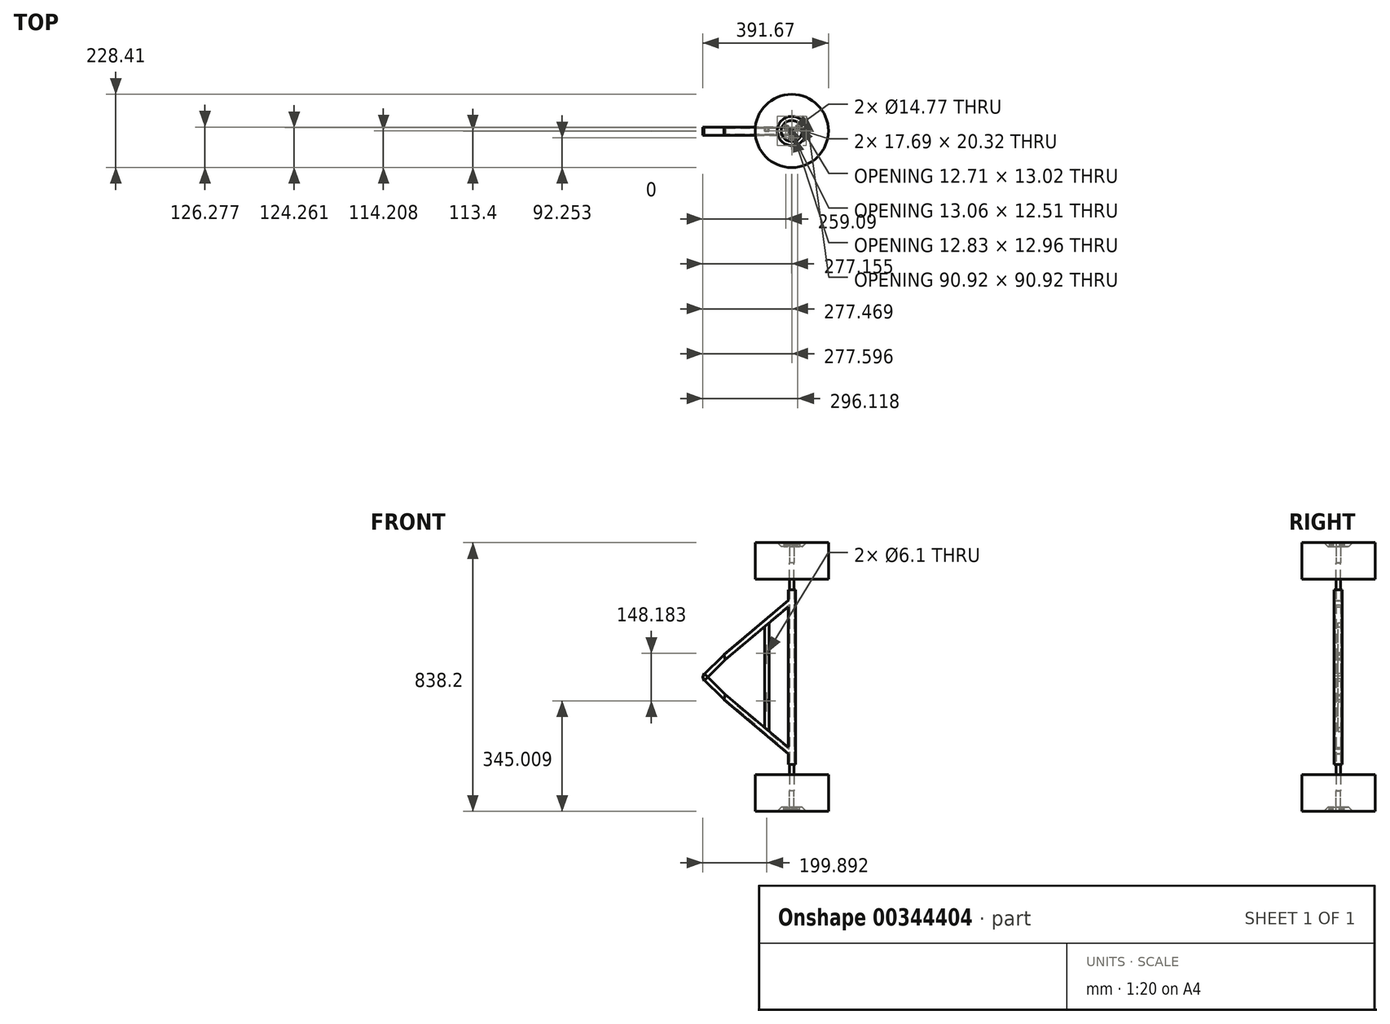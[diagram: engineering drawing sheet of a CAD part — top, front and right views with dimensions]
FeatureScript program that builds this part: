
annotation { "Feature Type Name" : "Feature", "Feature Type Description" : "" }
export const myFeature = defineFeature(function(context is Context, id is Id, definition is map)
    precondition{}
    {
        {
            var Q0;
            Q0=qCreatedBy(makeId("Front.planeOp"),FACE);
            var sketch = newSketch(context, id + "F0", { "sketchPlane" : qUnion([Q0])});
            skLineSegment(sketch, "E0", {"start": v(0, 0) * mm, "end": v(0, 258.28) * mm});
            skLineSegment(sketch, "E1", {"start": v(0, 258.28) * mm, "end": v(-222.38, 70.18) * mm});
            skLineSegment(sketch, "E2.MirrorCS", {"start": v(0, 0) * mm, "end": v(0, -258.28) * mm});
            skLineSegment(sketch, "E3.MirrorCS", {"start": v(0, -258.28) * mm, "end": v(-222.38, -70.18) * mm});
            skLineSegment(sketch, "E4", {"start": v(-22.77, 239.03) * mm, "end": v(-22.77, -239.03) * mm});
            skLineSegment(sketch, "E5", {"start": v(-218.72, 53.72) * mm, "end": v(-22.77, 219.42) * mm});
            skLineSegment(sketch, "E6.MirrorCS", {"start": v(-218.72, -53.72) * mm, "end": v(-22.77, -219.42) * mm});
            skLineSegment(sketch, "E7", {"start": v(-222.38, 70.18) * mm, "end": v(-218.72, 53.72) * mm});
            skLineSegment(sketch, "E8", {"start": v(-218.72, -53.72) * mm, "end": v(-222.38, -70.18) * mm});
            skLineSegment(sketch, "E9", {"start": v(-22.77, 239.03) * mm, "end": v(-22.77, 272.77) * mm});
            skLineSegment(sketch, "E10", {"start": v(-22.77, 272.77) * mm, "end": v(0, 272.77) * mm});
            skLineSegment(sketch, "E11", {"start": v(0, 272.77) * mm, "end": v(0, 258.28) * mm});
            skLineSegment(sketch, "E12.MirrorCS", {"start": v(-22.77, -272.77) * mm, "end": v(0, -272.77) * mm});
            skLineSegment(sketch, "E13.MirrorCS", {"start": v(-22.77, -239.03) * mm, "end": v(-22.77, -272.77) * mm});
            skLineSegment(sketch, "E14.MirrorCS", {"start": v(0, -272.77) * mm, "end": v(0, -258.28) * mm});
            skSolve(sketch);
        }
        {
            var Q0;
            Q0 = qSketchRegion(id + "F0", true);
            extrude(context, id + "F1", {"entities" : qUnion([Q0]), "depth" : 25.4 * mm});
        }
        {
            var Q0;
            Q0=makeQuery(id+"F1.opExtrude","SWEPT_FACE",FACE,{"disambiguationData":[OSD([sQuery(id+"F0.wireOp",EDGE,"E10")])]});
            var Q1;
            Q1=makeQuery(id+"F1.opExtrude","SWEPT_FACE",FACE,{"disambiguationData":[OSD([sQuery(id+"F0.wireOp",EDGE,"E12.MirrorCS")])]});
            shell(context, id + "F2", {"entities" : qUnion([Q0, Q1]), "thickness" : 2.54 * mm});
        }
        {
            var Q0;
            Q0=qCreatedBy(makeId("Top.planeOp"),FACE);
            var sketch = newSketch(context, id + "F3", { "sketchPlane" : qUnion([Q0])});
            skCircle(sketch, "E15", {"center": v(-11.51, -11.9) * mm, "radius": 7.39 * mm});
            skSolve(sketch);
        }
        {
            var Q0;
            Q0=makeQuery(id+"F3.imprint","IMPRINT",FACE,{"disambiguationData":[TD([[makeQuery(id+"F3.imprint","IMPRINT",EDGE,{"derivedFrom":sQuery(id+"F3.wireOp",EDGE,"E15")}),1.0]])]});
            var Q1;
            Q1=sQuery(id+"F3.wireOp",EDGE,"E15");
            extrude(context, id + "F4", {"entities" : qUnion([Q0]), "surfaceEntities" : qUnion([Q1]), "endBound" : BoundingType.SYMMETRIC, "depth" : 711.2 * mm});
        }
        {
            var Q0;
            Q0=makeQuery(id+"F4.opExtrude","CAP_FACE",FACE,{"disambiguationData":[OSD([sQuery(id+"F3.wireOp",EDGE,"E15")])],"isStart":false});
            var sketch = newSketch(context, id + "F5", { "sketchPlane" : qUnion([Q0])});
            skCircle(sketch, "E16", {"center": v(-11.51, -11.9) * mm, "radius": 32.76 * mm});
            skSolve(sketch);
        }
        {
            var Q0;
            Q0=makeQuery(id+"F5.imprint","IMPRINT",FACE,{"disambiguationData":[TD([[makeQuery(id+"F5.imprint","IMPRINT",EDGE,{"derivedFrom":sQuery(id+"F5.wireOp",EDGE,"E16")}),1.0]])]});
            extrude(context, id + "F6", {"entities" : qUnion([Q0]), "operationType" : NewBodyOperationType.ADD, "endBound" : BoundingType.SYMMETRIC, "depth" : 101.6 * mm});
        }
        {
            var Q0;
            Q0=makeQuery(id+"F4.opExtrude","CAP_FACE",FACE,{"disambiguationData":[OSD([sQuery(id+"F3.wireOp",EDGE,"E15")])],"isStart":false});
            var sketch = newSketch(context, id + "F7", { "sketchPlane" : qUnion([Q0])});
            skCircle(sketch, "E17", {"center": v(-11.51, -11.9) * mm, "radius": 7.38 * mm});
            skSolve(sketch);
        }
        {
            var Q0;
            Q0=makeQuery(id+"F7.imprint","IMPRINT",FACE,{"disambiguationData":[TD([[makeQuery(id+"F7.imprint","IMPRINT",EDGE,{"derivedFrom":sQuery(id+"F7.wireOp",EDGE,"E17")}),1.0]])]});
            extrude(context, id + "F8", {"entities" : qUnion([Q0]), "operationType" : NewBodyOperationType.ADD, "depth" : 63.5 * mm});
        }
        {
            var Q0;
            Q0=makeQuery(id+"F6.opExtrude","CAP_FACE",FACE,{"disambiguationData":[OSD([sQuery(id+"F3.wireOp",EDGE,"E15"),sQuery(id+"F5.wireOp",EDGE,"E16")])],"isStart":false});
            var sketch = newSketch(context, id + "F9", { "sketchPlane" : qUnion([Q0])});
            skCircle(sketch, "E18.cCircle", {"center": v(-12.22, -33.58) * mm, "radius": 5.56 * mm, "construction": true});
            skLineSegment(sketch, "E18.0", {"start": v(-9.3, -27.37) * mm, "end": v(-5.4, -34.45) * mm});
            skLineSegment(sketch, "E18.1", {"start": v(-5.4, -34.45) * mm, "end": v(-10.94, -40.33) * mm});
            skLineSegment(sketch, "E18.2", {"start": v(-10.94, -40.33) * mm, "end": v(-18.24, -36.88) * mm});
            skLineSegment(sketch, "E18.3", {"start": v(-18.24, -36.88) * mm, "end": v(-17.22, -28.87) * mm});
            skLineSegment(sketch, "E18.4", {"start": v(-17.22, -28.87) * mm, "end": v(-9.3, -27.37) * mm});
            skPoint(sketch, "E18.0.midPoint", {"position": v(-7.35, -30.9) * mm});
            skLineSegment(sketch, "E19.1.0", {"start": v(-26.02, -6.08) * mm, "end": v(-34.1, -5.9) * mm});
            skLineSegment(sketch, "E19.1.1", {"start": v(-23.36, 1.54) * mm, "end": v(-26.02, -6.08) * mm});
            skCircle(sketch, "E19.1.2", {"center": v(-29.94, -0.43) * mm, "radius": 5.56 * mm, "construction": true});
            skLineSegment(sketch, "E19.1.3", {"start": v(-29.79, 6.43) * mm, "end": v(-23.36, 1.54) * mm});
            skLineSegment(sketch, "E19.1.4", {"start": v(-36.42, 1.83) * mm, "end": v(-29.79, 6.43) * mm});
            skLineSegment(sketch, "E19.1.5", {"start": v(-34.1, -5.9) * mm, "end": v(-36.42, 1.83) * mm});
            skLineSegment(sketch, "E19.2.0", {"start": v(0.78, -2.23) * mm, "end": v(4.97, 4.67) * mm});
            skLineSegment(sketch, "E19.2.1", {"start": v(6.05, -8.35) * mm, "end": v(0.78, -2.23) * mm});
            skCircle(sketch, "E19.2.2", {"center": v(7.63, -1.66) * mm, "radius": 5.56 * mm, "construction": true});
            skLineSegment(sketch, "E19.2.3", {"start": v(13.5, -5.23) * mm, "end": v(6.05, -8.35) * mm});
            skLineSegment(sketch, "E19.2.4", {"start": v(12.83, 2.82) * mm, "end": v(13.5, -5.23) * mm});
            skLineSegment(sketch, "E19.2.5", {"start": v(4.97, 4.67) * mm, "end": v(12.83, 2.82) * mm});
            skPoint(sketch, "E19.center", {"position": v(-11.51, -11.9) * mm});
            skLineSegment(sketch, "E19.anchor1", {"start": v(-11.51, -11.9) * mm, "end": v(-5.4, -34.45) * mm, "construction": true});
            skLineSegment(sketch, "E19.anchor2", {"start": v(-11.51, -11.9) * mm, "end": v(4.97, 4.67) * mm, "construction": true});
            skSolve(sketch);
        }
        {
            var Q0;
            Q0=makeQuery(id+"F9.imprint","IMPRINT",FACE,{"disambiguationData":[TD([[makeQuery(id+"F9.imprint","IMPRINT",EDGE,{"derivedFrom":sQuery(id+"F9.wireOp",EDGE,"E18.0")}),-1.0]])]});
            var Q1;
            Q1=makeQuery(id+"F9.imprint","IMPRINT",FACE,{"disambiguationData":[TD([[makeQuery(id+"F9.imprint","IMPRINT",EDGE,{"derivedFrom":sQuery(id+"F9.wireOp",EDGE,"E19.2.0")}),-1.0]])]});
            var Q2;
            Q2=makeQuery(id+"F9.imprint","IMPRINT",FACE,{"disambiguationData":[TD([[makeQuery(id+"F9.imprint","IMPRINT",EDGE,{"derivedFrom":sQuery(id+"F9.wireOp",EDGE,"E19.1.0")}),-1.0]])]});
            extrude(context, id + "F10", {"entities" : qUnion([Q0, Q1, Q2]), "operationType" : NewBodyOperationType.ADD, "depth" : 7.62 * mm});
        }
        {
            var Q0;
            Q0=makeQuery(id+"F6.opExtrude","CAP_FACE",FACE,{"disambiguationData":[OSD([sQuery(id+"F3.wireOp",EDGE,"E15"),sQuery(id+"F5.wireOp",EDGE,"E16")])],"isStart":true});
            var sketch = newSketch(context, id + "F11", { "sketchPlane" : qUnion([Q0])});
            skCircle(sketch, "E20", {"center": v(-11.51, 11.9) * mm, "radius": 114.2 * mm});
            skCircle(sketch, "E21", {"center": v(-11.51, 11.9) * mm, "radius": 90.4 * mm});
            skSolve(sketch);
        }
        {
            var Q0;
            Q0=makeQuery(id+"F11.imprint","IMPRINT",FACE,{"disambiguationData":[TD([[makeQuery(id+"F11.imprint","IMPRINT",EDGE,{"derivedFrom":sQuery(id+"F11.wireOp",EDGE,"E20")}),1.0]])]});
            var Q1;
            Q1=makeQuery(id+"F11.imprint","IMPRINT",FACE,{"disambiguationData":[TD([[makeQuery(id+"F11.imprint","IMPRINT",EDGE,{"derivedFrom":sQuery(id+"F11.wireOp",EDGE,"E21")}),1.0]])]});
            extrude(context, id + "F12", {"entities" : qUnion([Q0, Q1]), "operationType" : NewBodyOperationType.ADD, "oppositeDirection" : true, "depth" : 114.3 * mm});
        }
        {
            var Q0;
            Q0=makeQuery(id+"F12.opExtrude","CAP_EDGE",EDGE,{"disambiguationData":[OSD([sQuery(id+"F5.wireOp",EDGE,"E16")])],"isStart":false});
            chamfer(context, id + "F13", {"entities" : qUnion([Q0]), "width" : 12.7 * mm, "tangentPropagation" : true});
        }
        {
            var Q0;
            Q0=makeQuery(id+"F4.opExtrude","SWEPT_BODY",BODY,{"disambiguationData":[OSD([sQuery(id+"F3.wireOp",EDGE,"E15")])]});
            var Q1;
            Q1=qCreatedBy(makeId("Top.planeOp"),FACE);
            mirror(context, id + "F14", {"operationType" : NewBodyOperationType.ADD, "entities" : qUnion([Q0]), "mirrorPlane" : qUnion([Q1])});
        }
        {
            var Q0;
            Q0=qCreatedBy(makeId("Front.planeOp"),FACE);
            var sketch = newSketch(context, id + "F15", { "sketchPlane" : qUnion([Q0])});
            skLineSegment(sketch, "E22", {"start": v(-221.44, 66.17) * mm, "end": v(-288.08, 0) * mm});
            skLineSegment(sketch, "E23.MirrorCS", {"start": v(-221.44, -66.17) * mm, "end": v(-288.08, 0) * mm});
            skSolve(sketch);
        }
        {
            var Q0;
            Q0=makeQuery(id+"F1.opExtrude","SWEPT_FACE",FACE,{"disambiguationData":[OSD([sQuery(id+"F0.wireOp",EDGE,"E7")])]});
            var Q1;
            Q1=sQuery(id+"F15.wireOp",EDGE,"E22");
            sweep(context, id + "F16", {"operationType" : NewBodyOperationType.ADD, "profiles" : qUnion([Q0]), "path" : qUnion([Q1])});
        }
        {
            var Q0;
            Q0=makeQuery(id+"F1.opExtrude","SWEPT_BODY",BODY,{"disambiguationData":[OSD([sQuery(id+"F0.wireOp",EDGE,"E0"),sQuery(id+"F0.wireOp",EDGE,"E1"),sQuery(id+"F0.wireOp",EDGE,"E2.MirrorCS"),sQuery(id+"F0.wireOp",EDGE,"E3.MirrorCS"),sQuery(id+"F0.wireOp",EDGE,"E4"),sQuery(id+"F0.wireOp",EDGE,"E5"),sQuery(id+"F0.wireOp",EDGE,"E6.MirrorCS"),sQuery(id+"F0.wireOp",EDGE,"E7"),sQuery(id+"F0.wireOp",EDGE,"E8"),sQuery(id+"F0.wireOp",EDGE,"E9"),sQuery(id+"F0.wireOp",EDGE,"E10"),sQuery(id+"F0.wireOp",EDGE,"E11"),sQuery(id+"F0.wireOp",EDGE,"E12.MirrorCS"),sQuery(id+"F0.wireOp",EDGE,"E13.MirrorCS"),sQuery(id+"F0.wireOp",EDGE,"E14.MirrorCS")])]});
            var Q1;
            Q1=qCreatedBy(makeId("Top.planeOp"),FACE);
            mirror(context, id + "F17", {"entities" : qUnion([Q0]), "mirrorPlane" : qUnion([Q1])});
        }
        {
            var Q0;
            Q0=qCreatedBy(makeId("Front.planeOp"),FACE);
            var sketch = newSketch(context, id + "F18", { "sketchPlane" : qUnion([Q0])});
            skLineSegment(sketch, "E24", {"start": v(-82.14, -169.23) * mm, "end": v(-82.14, 0) * mm});
            skLineSegment(sketch, "E25", {"start": v(-96.27, -156.85) * mm, "end": v(-96.27, 0) * mm});
            skLineSegment(sketch, "E26", {"start": v(-96.27, -156.85) * mm, "end": v(-82.14, -169.23) * mm});
            skLineSegment(sketch, "E27.MirrorCS", {"start": v(-82.14, 169.23) * mm, "end": v(-82.14, 0) * mm});
            skLineSegment(sketch, "E28.MirrorCS", {"start": v(-96.27, 156.85) * mm, "end": v(-96.27, 0) * mm});
            skLineSegment(sketch, "E29.MirrorCS", {"start": v(-96.27, 156.85) * mm, "end": v(-82.14, 169.23) * mm});
            skSolve(sketch);
        }
        {
            var Q0;
            Q0=makeQuery(id+"F18.imprint","IMPRINT",FACE,{"disambiguationData":[TD([[makeQuery(id+"F18.imprint","IMPRINT",EDGE,{"derivedFrom":sQuery(id+"F18.wireOp",EDGE,"E24")}),1.0]])]});
            extrude(context, id + "F19", {"entities" : qUnion([Q0]), "depth" : 12.7 * mm});
        }
        {
            var Q0;
            Q0=makeQuery(id+"F19.opExtrude","CAP_FACE",FACE,{"disambiguationData":[OSD([sQuery(id+"F18.wireOp",EDGE,"E24"),sQuery(id+"F18.wireOp",EDGE,"E25"),sQuery(id+"F18.wireOp",EDGE,"E26"),sQuery(id+"F18.wireOp",EDGE,"E27.MirrorCS"),sQuery(id+"F18.wireOp",EDGE,"E28.MirrorCS"),sQuery(id+"F18.wireOp",EDGE,"E29.MirrorCS")])],"isStart":true});
            var sketch = newSketch(context, id + "F20", { "sketchPlane" : qUnion([Q0])});
            skCircle(sketch, "E30", {"center": v(89.09, -74.1) * mm, "radius": 3.08 * mm});
            skCircle(sketch, "E31.MirrorC", {"center": v(89.09, 74.1) * mm, "radius": 3.08 * mm});
            skSolve(sketch);
        }
        {
            var Q0;
            Q0=sQuery(id+"F20.wireOp",VERTEX,"E30.center");
            var Q1;
            Q1=sQuery(id+"F20.wireOp",VERTEX,"E31.MirrorC.center");
            var Q2;
            Q2=makeQuery(id+"F19.opExtrude","SWEPT_BODY",BODY,{"disambiguationData":[OSD([sQuery(id+"F18.wireOp",EDGE,"E24"),sQuery(id+"F18.wireOp",EDGE,"E25"),sQuery(id+"F18.wireOp",EDGE,"E26"),sQuery(id+"F18.wireOp",EDGE,"E27.MirrorCS"),sQuery(id+"F18.wireOp",EDGE,"E28.MirrorCS"),sQuery(id+"F18.wireOp",EDGE,"E29.MirrorCS")])]});
            hole(context, id + "F21", {"style" : HoleStyle.SIMPLE, "endStyle" : HoleEndStyle.THROUGH, "holeDiameter" : 6.1 * mm, "isTappedThrough" : true, "tappedDepth" : 12.7 * mm, "tapClearance" : 3, "locations" : qUnion([Q0, Q1]), "scope" : qUnion([Q2])});
        }
    });
